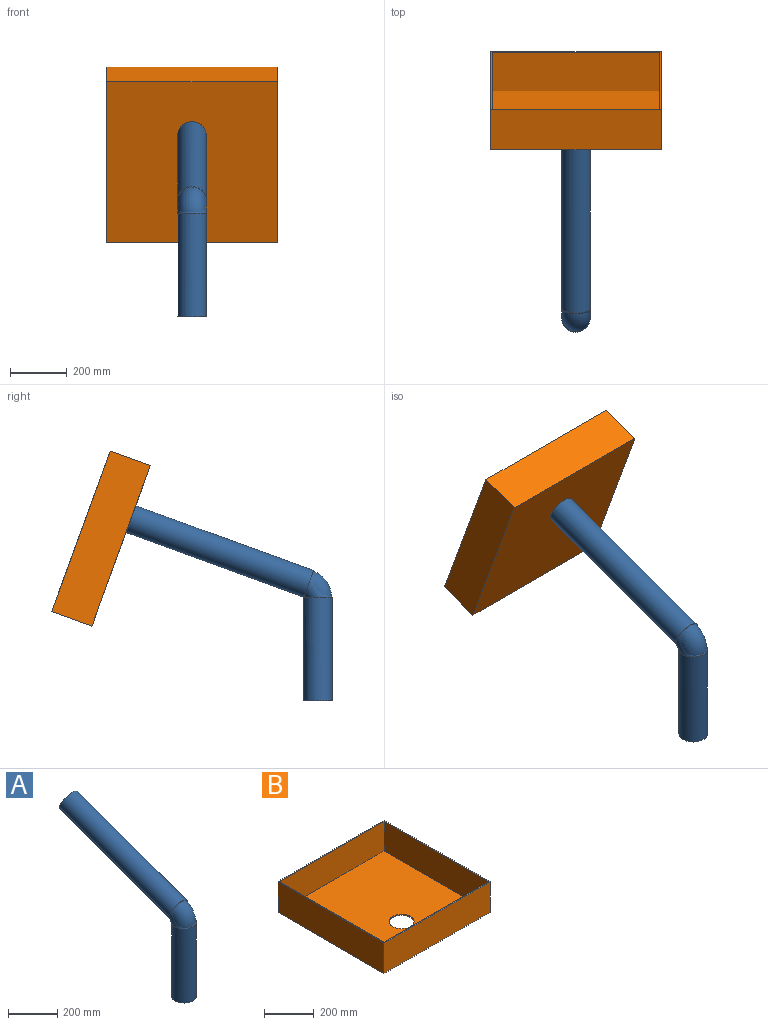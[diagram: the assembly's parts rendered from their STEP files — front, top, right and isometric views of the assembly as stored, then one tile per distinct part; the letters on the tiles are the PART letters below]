
ASSEMBLY  parts=2 mates=1
PART A: 8 faces, bbox 100x733.1x686.4 mm
  f0: plane 100x100mm, normal (0,0,-1), area 765.8mm2, adj f2,f5
  f1: plane 100x93.97mm, normal (0,0.94,0.34), area 765.8mm2, adj f4,f7
  f2: cylinder r=50mm len=364.99mm, axis (0,0,1), area 114664.9mm2, adj f0,f3
  f3: torus R=50mm, axis (-1,0,0), area 19190.9mm2, adj f2,f4
  f4: cylinder r=50mm len=659.09mm, axis (0,0.94,0.34), area 208912.7mm2, adj f1,f3
  f5: cylinder r=47.5mm len=364.99mm, axis (0,0,1), area 108931.6mm2, adj f0,f6
  f6: torus R=50mm, axis (-1,0,0), area 18231.4mm2, adj f5,f7
  f7: cylinder r=47.5mm len=657.38mm, axis (0,0.94,0.34), area 198467mm2, adj f1,f6
PART B: 12 faces, bbox 600x600x150 mm
  f0: plane 600x600mm, normal (0,0,1), area 11900mm2, adj f1,f2,f3,f4,f6,f7,f8,f9
  f1: plane 600x150mm, normal (0,1,0), area 90000mm2, adj f0,f2,f4,f5
  f2: plane 600x150mm, normal (-1,0,0), area 90000mm2, adj f0,f1,f3,f5
  f3: plane 600x150mm, normal (0,-1,0), area 90000mm2, adj f0,f2,f4,f5
  f4: plane 600x150mm, normal (1,0,0), area 90000mm2, adj f0,f1,f3,f5
  f5: plane 600x600mm, normal (0,0,-1), area 352146mm2, adj f1,f2,f3,f4,f11
  f6: plane 590x145mm, normal (0,-1,0), area 85550mm2, adj f0,f7,f9,f10
  f7: plane 590x145mm, normal (1,0,0), area 85550mm2, adj f0,f6,f8,f10
  f8: plane 590x145mm, normal (0,1,0), area 85550mm2, adj f0,f7,f9,f10
  f9: plane 590x145mm, normal (-1,0,0), area 85550mm2, adj f0,f6,f8,f10
  f10: plane 590x590mm, normal (0,0,1), area 340246mm2, adj f6,f7,f8,f9,f11
  f11: cylinder r=50mm len=100mm, axis (0,0,-1), area 1570.8mm2, adj f5,f10
PLACE A t=(-145.73,-312.43,-313.6)mm
PLACE B rot(axis=(-1,0,0),70deg) t=(-145.73,379.55,231.84)mm
MATE fastened B.f11 <-> A.f4  axis (0,-0.94,-0.34) through (-145.73,345.35,325.81)mm
